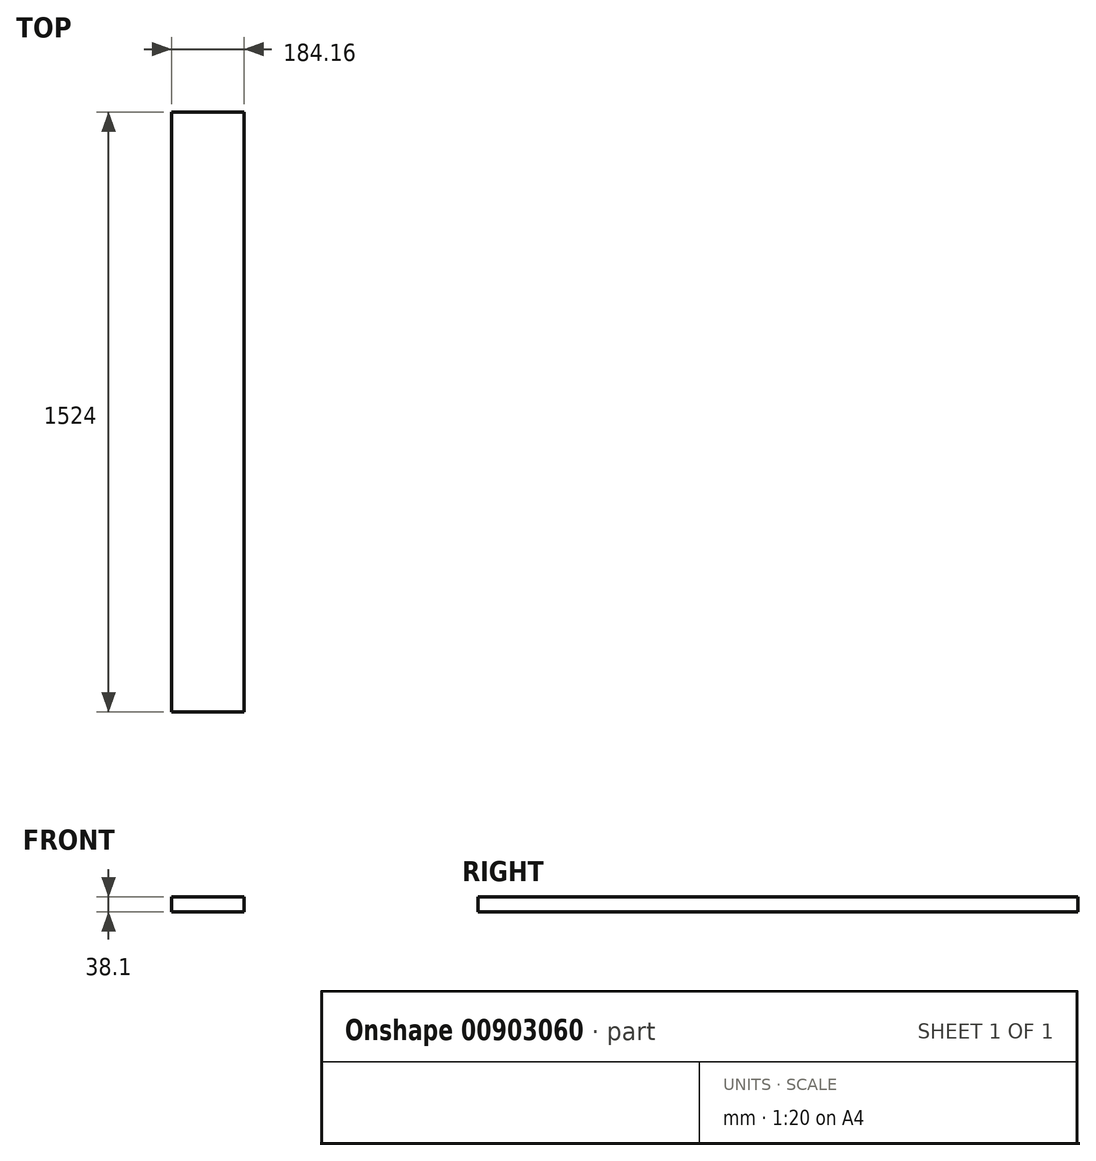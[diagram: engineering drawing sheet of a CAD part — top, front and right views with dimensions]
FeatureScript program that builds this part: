
annotation { "Feature Type Name" : "Feature", "Feature Type Description" : "" }
export const myFeature = defineFeature(function(context is Context, id is Id, definition is map)
    precondition{}
    {
        {
            var Q0;
            Q0=qCreatedBy(makeId("Front.planeOp"),FACE);
            var sketch = newSketch(context, id + "F0", { "sketchPlane" : qUnion([Q0])});
            skLineSegment(sketch, "E0.bottom", {"start": v(92.08, 19.05) * mm, "end": v(-92.08, 19.05) * mm});
            skLineSegment(sketch, "E0.top", {"start": v(92.08, -19.05) * mm, "end": v(-92.08, -19.05) * mm});
            skLineSegment(sketch, "E0.left", {"start": v(92.08, 19.05) * mm, "end": v(92.08, -19.05) * mm});
            skLineSegment(sketch, "E0.right", {"start": v(-92.08, 19.05) * mm, "end": v(-92.08, -19.05) * mm});
            skPoint(sketch, "E0.middle", {"position": v(0, 0) * mm});
            skSolve(sketch);
        }
        {
            var Q0;
            Q0=makeQuery(id+"F0.imprint","IMPRINT",FACE,{"disambiguationData":[TD([[makeQuery(id+"F0.imprint","IMPRINT",EDGE,{"derivedFrom":sQuery(id+"F0.wireOp",EDGE,"E0.bottom")}),1.0]])]});
            extrude(context, id + "F1", {"entities" : qUnion([Q0]), "depth" : 1524 * mm, "offsetDistance" : 25.4 * mm});
        }
    });
